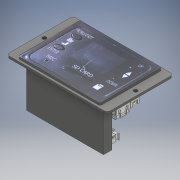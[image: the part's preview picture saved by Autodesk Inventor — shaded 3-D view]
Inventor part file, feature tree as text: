
AUTODESK INVENTOR PART (.ipt)
format: ipt  version: 2017 (Build 210142000, 142)  size: 6,165,504 bytes
history: native  units: mm
features: other x28, sketch x10, extrude x4, fillet x1, hole x1
ambient origin geometry x8: Origin, YZ Plane, XZ Plane, XY Plane, X Axis, Y Axis, Z Axis, Center Point
bodies: Solide1 (feature_tree), Solide2 (feature_tree), Solide3 (feature_tree), Solide5 (feature_tree), Solide6 (feature_tree), Solide7 (feature_tree), Solide8 (feature_tree), Solide9 (feature_tree), Solide10 (feature_tree), Solide11 (feature_tree), Solide12 (feature_tree)
feature tree (44):
  other  "Connecteur jst 2 broches.iam"
  other  "Connecteur jst 3 broches.iam"
  other  "Connecteur jst 4 broches.iam"
  other  "Connecteur jst 5 broches.iam"
  other  "Connecteur jst 2 broches femelle.ipt:1"
  other  "Connecteur JST 2 Broches Male.ipt:1"
  other  "Connecteur jst 3 broches femelle.ipt:1"
  other  "Connecteur JST 3 Broches Male.ipt:1"
  other  "Connecteur jst 4 broches femelle.ipt:1"
  other  "Connecteur JST 4 Broches Male.ipt:1"
  other  "Connecteur jst 5 broches femelle.ipt:1"
  other  "Connecteur JST 5 Broches Male.ipt:1"
  extrude  "Extrusion1"  Depth=90.8mm
  extrude  "Extrusion2"  Depth=59.8mm
  fillet  "Congé1"  Radius=2.0mm
  extrude  "Extrusion3"  Depth=73.8mm
  extrude  "Extrusion5"  Depth=55.8mm
  hole  "Perçage1"  [1 undecoded]
  other  "Décalcomanie1"
  other  "Décalcomanie2"
  other  "Décalcomanie3"
  other  "Déplacer des corps1"
  other  "Déplacer des corps3"
  other  "Déplacer des corps4"
  other  "Déplacer des corps5"
  other  "Déplacer des corps6"
  other  "Déplacer des corps7"
  other  "Déplacer des corps8"
  other  "Déplacer des corps9"
  other  "Déplacer des corps10"
  other  "Combiner1"
  sketch  "Esquisse11"
  sketch  "Esquisse12"
  sketch  "Esquisse1"
  sketch  "Esquisse2"
  sketch  "Esquisse3"
  sketch  "Esquisse5"
  sketch  "Esquisse6"
  sketch  "Esquisse7"
  other  "Image1"
  sketch  "Esquisse8"
  other  "Image2"
  sketch  "Esquisse9"
  other  "Image3"
note: 1 required parameter value undecoded (feature->parameter linkage not recoverable at this tier; creation-order binding heuristic only, values carry confidence <= 0.55)
